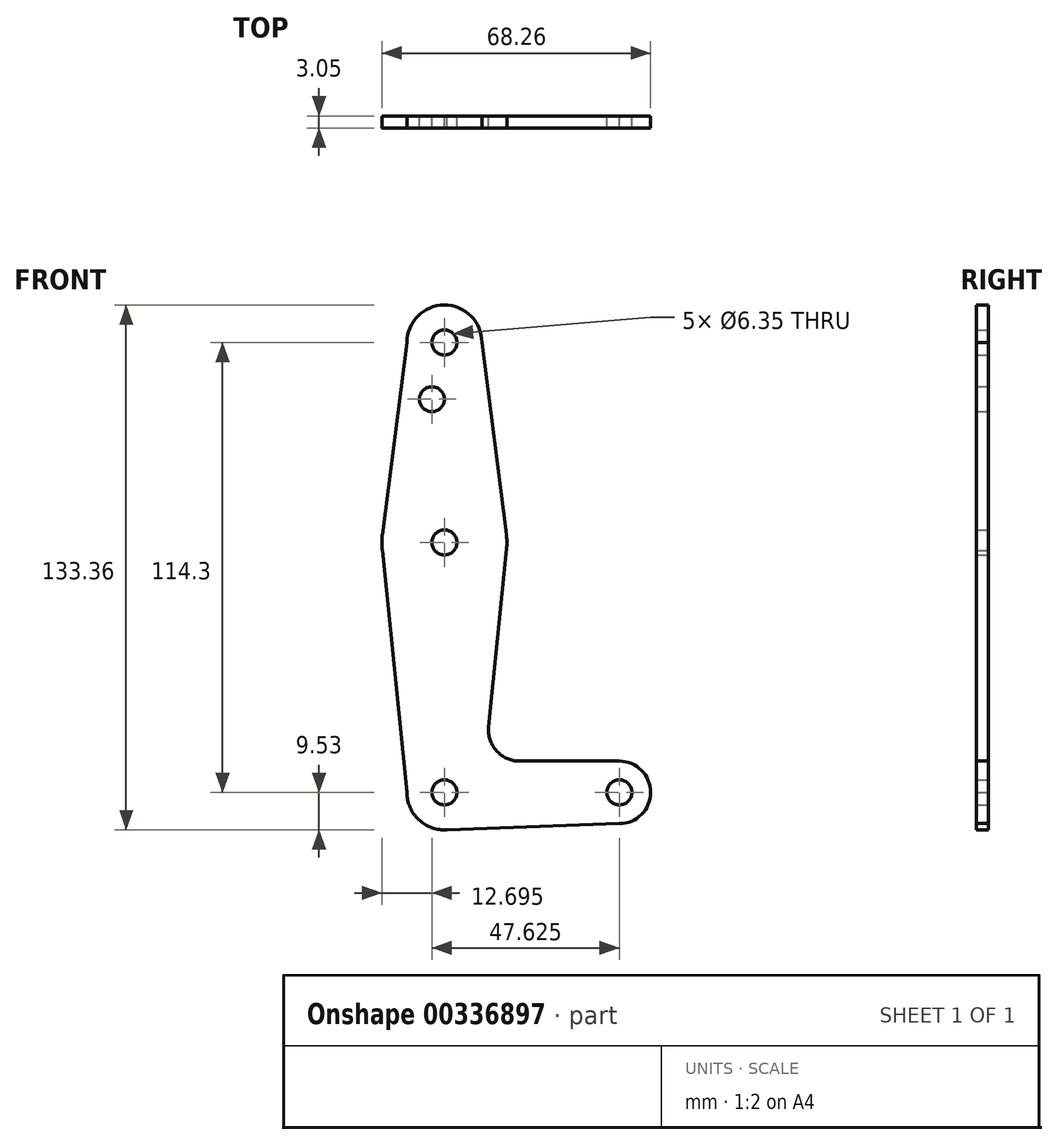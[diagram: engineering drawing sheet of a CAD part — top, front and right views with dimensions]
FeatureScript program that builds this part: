
annotation { "Feature Type Name" : "Feature", "Feature Type Description" : "" }
export const myFeature = defineFeature(function(context is Context, id is Id, definition is map)
    precondition{}
    {
        {
            var Q0;
            Q0=qCreatedBy(makeId("Front.planeOp"),FACE);
            var sketch = newSketch(context, id + "F0", { "sketchPlane" : qUnion([Q0])});
            skLineSegment(sketch, "E0", {"start": v(0, 114.3) * mm, "end": v(0, 0) * mm, "construction": true});
            skLineSegment(sketch, "E1", {"start": v(0, 0) * mm, "end": v(44.45, 0) * mm, "construction": true});
            skCircle(sketch, "E2", {"center": v(0, 114.3) * mm, "radius": 9.53 * mm});
            skCircle(sketch, "E3", {"center": v(0, 0) * mm, "radius": 9.53 * mm});
            skCircle(sketch, "E4", {"center": v(0, 63.5) * mm, "radius": 15.88 * mm});
            skCircle(sketch, "E5", {"center": v(44.45, 0) * mm, "radius": 7.94 * mm});
            skLineSegment(sketch, "E6", {"start": v(-9.53, 114.3) * mm, "end": v(-15.75, 65.5) * mm});
            skLineSegment(sketch, "E7", {"start": v(9.52, 114.3) * mm, "end": v(15.75, 65.5) * mm});
            skLineSegment(sketch, "E8", {"start": v(0, -9.52) * mm, "end": v(44.45, -7.94) * mm});
            skCircle(sketch, "E9", {"center": v(0, 114.3) * mm, "radius": 3.18 * mm});
            skCircle(sketch, "E10", {"center": v(0, 63.5) * mm, "radius": 3.18 * mm});
            skCircle(sketch, "E11", {"center": v(0, 0) * mm, "radius": 3.18 * mm});
            skCircle(sketch, "E12", {"center": v(44.45, 0) * mm, "radius": 3.18 * mm});
            skCircle(sketch, "E13", {"center": v(-3.17, 99.89) * mm, "radius": 3.18 * mm});
            skLineSegment(sketch, "E14", {"start": v(-9.53, 0) * mm, "end": v(-15.75, 61.5) * mm});
            skLineSegment(sketch, "E15", {"start": v(11.22, 16.69) * mm, "end": v(15.8, 61.9) * mm});
            skLineSegment(sketch, "E16", {"start": v(19.12, 7.94) * mm, "end": v(44.45, 7.94) * mm});
            skArc(sketch, "E17.filletArc", {"start": v(11.22, 16.69) * mm, "mid": v(13.23, 10.56) * mm, "end": v(19.12, 7.94) * mm});
            skSolve(sketch);
        }
        {
            var Q0;
            Q0 = qSketchRegion(id + "F0", true);
            extrude(context, id + "F1", {"entities" : qUnion([Q0]), "depth" : 3.05 * mm});
        }
    });
